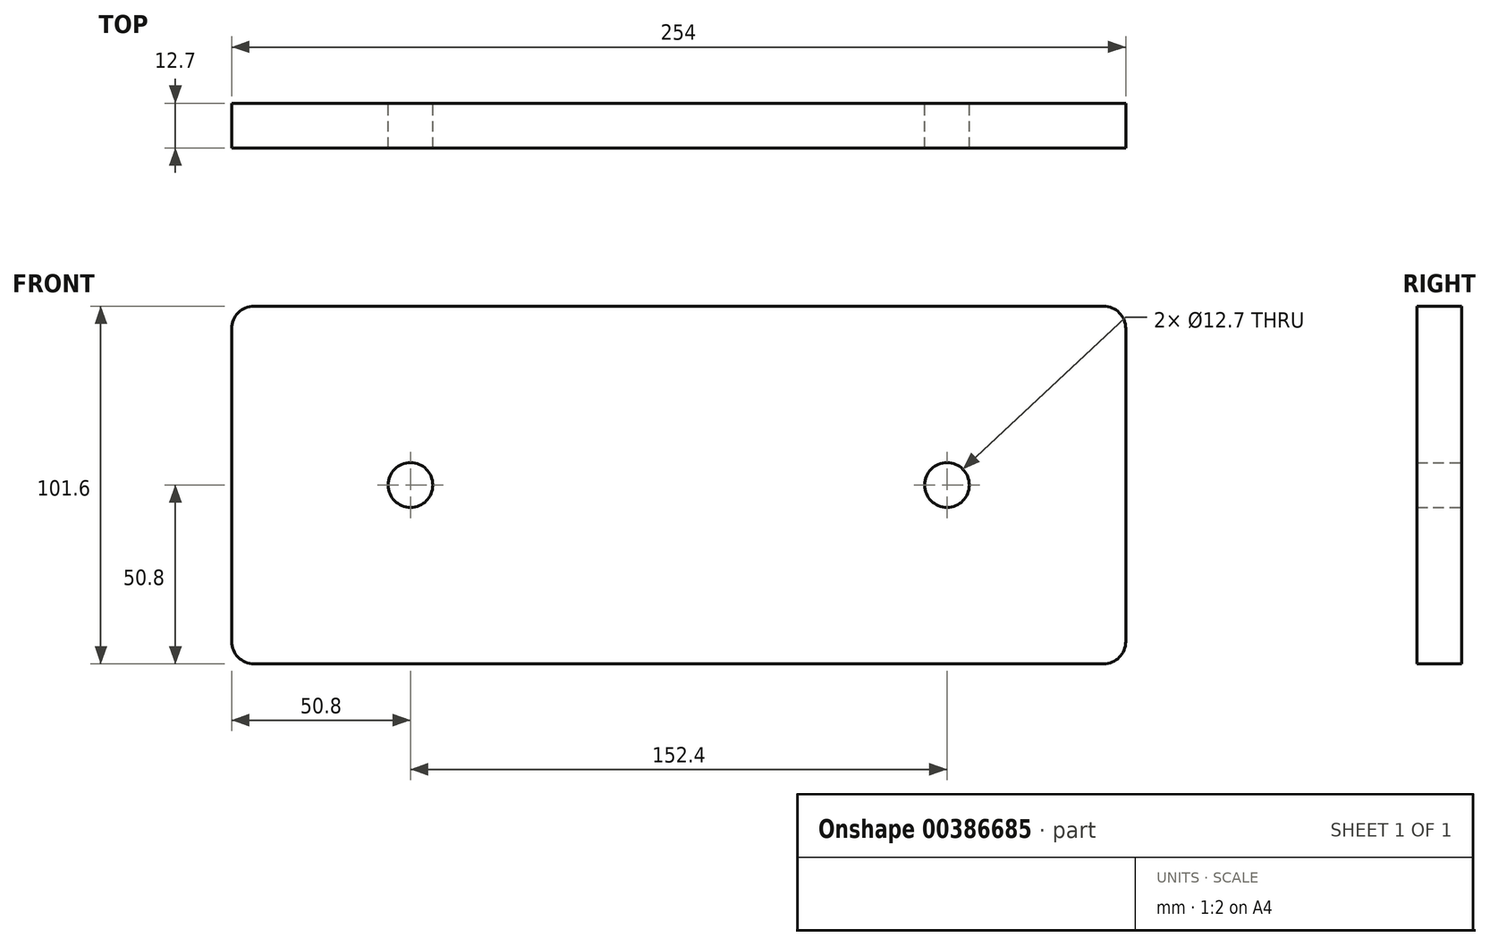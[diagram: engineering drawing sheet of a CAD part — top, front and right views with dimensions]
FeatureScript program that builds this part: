
annotation { "Feature Type Name" : "Feature", "Feature Type Description" : "" }
export const myFeature = defineFeature(function(context is Context, id is Id, definition is map)
    precondition{}
    {
        {
            var Q0;
            Q0=qCreatedBy(makeId("Front.planeOp"),FACE);
            var sketch = newSketch(context, id + "F0", { "sketchPlane" : qUnion([Q0])});
            skLineSegment(sketch, "E0.bottom", {"start": v(6.35, 0) * mm, "end": v(247.65, 0) * mm});
            skLineSegment(sketch, "E0.top", {"start": v(6.35, 101.6) * mm, "end": v(247.65, 101.6) * mm});
            skLineSegment(sketch, "E0.left", {"start": v(0, 6.35) * mm, "end": v(0, 95.25) * mm});
            skLineSegment(sketch, "E0.right", {"start": v(254, 6.35) * mm, "end": v(254, 95.25) * mm});
            skCircle(sketch, "E1", {"center": v(50.8, 50.8) * mm, "radius": 6.35 * mm});
            skCircle(sketch, "E2", {"center": v(203.2, 50.8) * mm, "radius": 6.35 * mm});
            skPoint(sketch, "E3.visualSharp", {"position": v(254, 101.6) * mm});
            skArc(sketch, "E3.filletArc", {"start": v(254, 95.25) * mm, "mid": v(252.14, 99.74) * mm, "end": v(247.65, 101.6) * mm});
            skPoint(sketch, "E4.visualSharp", {"position": v(254, 0) * mm});
            skArc(sketch, "E4.filletArc", {"start": v(247.65, 0) * mm, "mid": v(252.14, 1.86) * mm, "end": v(254, 6.35) * mm});
            skPoint(sketch, "E5.visualSharp", {"position": v(0, 0) * mm});
            skArc(sketch, "E5.filletArc", {"start": v(0, 6.35) * mm, "mid": v(1.86, 1.86) * mm, "end": v(6.35, 0) * mm});
            skPoint(sketch, "E6.visualSharp", {"position": v(0, 101.6) * mm});
            skArc(sketch, "E6.filletArc", {"start": v(6.35, 101.6) * mm, "mid": v(1.86, 99.74) * mm, "end": v(0, 95.25) * mm});
            skSolve(sketch);
        }
        {
            var Q0;
            Q0=makeQuery(id+"F0.imprint","IMPRINT",FACE,{"disambiguationData":[TD([[makeQuery(id+"F0.imprint","IMPRINT",EDGE,{"derivedFrom":sQuery(id+"F0.wireOp",EDGE,"E0.bottom")}),1.0]])]});
            extrude(context, id + "F1", {"entities" : qUnion([Q0]), "depth" : 12.7 * mm});
        }
    });
